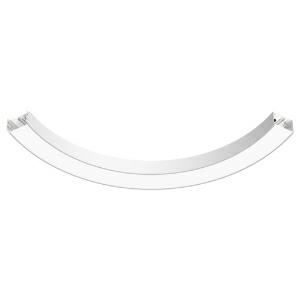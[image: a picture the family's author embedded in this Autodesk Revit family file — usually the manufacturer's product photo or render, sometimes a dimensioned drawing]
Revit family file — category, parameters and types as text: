
# Revit family: super-g_super-g__2100___120deg_ab_led__32_2w_4970lm_3000k_cri_80_350-1010_6d97
name_source: partatom
category: Leuchten
revit_build: Autodesk Revit 2016 (Build: 20190508_0715(x64)
units: mm (PartAtom-declared; Revit-internal decimal feet)

## family parameters
Basisbauteil = Fläche
Beim Laden mit Abzugskörper schneiden = Nein
Bemaßung runder Anschluss = Durchmesser verwenden
Gemeinsam genutzt = Nein
Lichtquelle = Nein
Raumberechnungspunkt = Nein
Teiletyp = Normal

## types (1)
- 350-1010- (1 x LED, 710 lm, 3000K)
    Approval mark = CE
    Beschreibung = The insert consists of aluminum-extruded profile. Charming SOFT-EDGE design ensure unparalleled styling. The ballast is integrated and allows for an operation with 220-240V (50/60Hz). SUPER-G (# 350-1010) ist not dimmable (on/off).
    CIE Flux Codes = 44 75 94 100 65
    Color Rendering = 1B/80…89
    Color Temperature = 3000K
    Height = 120 mm
    Hersteller = Prolicht
    Lamp Light Flux = 710 lm
    Lamp count = 1
    Lampe = 1 x LED
    Length = 314 mm
    Luminous efficacy = 90 lm/W
    ModVariant = Nein
    Modell = 350-1010
    Mounting Place = Ceiling
    Mounting Type = Surface mounted
    Number of Poles = 1
    OnlyDefault = Ja
    Power Factor = 1
    Product Name = SUPER-G__SUPER-G  2100 / 120° AB LED: 32,2W 4970lm 3000K CRI:80
    Product group = Surface profile systems
    ProductGroupID = 335
    Protection Class = Protection class I
    Protection Degree = IP 20
    RLX_Detail_Level = 1
    RlxData = <blob elided: 29449 chars, md5=e51a3523>
    Scheinlast = 36 VA
    Socket = socket
    Standby Power = 0 W
    System Light Flux = 3231 lm
    System Power = 36 W
    Typenbild = 350-1010.jpg
    URL = http://relux.com
    VarID = 350-1010-
    Voltage = 0 V
    Vorgabe-Ansicht = 1800 mm
    Weight = 0.00 kg
    Width = 150 mm

## geometry (parser evidence)
native form markers: Blend x4, Sweep x26
no freeform markers — native parametric forms only
